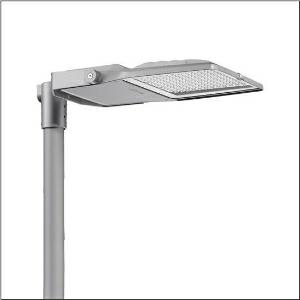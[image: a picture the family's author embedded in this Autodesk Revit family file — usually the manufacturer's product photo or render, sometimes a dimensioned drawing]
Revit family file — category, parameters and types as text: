
# Revit family: floodlight_fl_21_midi___pl64_5xa7785e2e3a_0c5c
name_source: partatom
category: Lighting Fixtures
units: mm (PartAtom-declared; Revit-internal decimal feet)

## family parameters
Cut with Voids When Loaded = No
Host = Face
Light Source = No
Part Type = Normal
Room Calculation Point = No
Round Connector Dimension = Use Diameter
Shared = No

## types (1)
- --- (1 x LED, 26020 lm, 212.4 W, 3000K)
    Apparent Load = 212 VA
    CIE Flux Codes = 28 80 98 100 100
    Color Rendering = 70
    Color Temperature = 3000K
    Default Elevation = 1800 mm
    Description = Floodlight FL 21 midi, floodlight, primary light control with lens, of PMMA, primary optical cover: protective disc, of toughened safety glass, transparent, light distribution: PL64, light emission: direct distribution, installation type: surface-mounted, LED, High Power LED, rated luminous flux: 26.020lm, luminous efficacy: 123lm/W, light colour: 730, colour temperature: 3000K, control gear: Smart Interface (Zhaga), control: flexible luminous flux parameterisation, time-dependent luminous flux control, constant luminous flux control, overheat protection, pre-setting: logarithmic dimming characteristic, with terminal, 6-pole, mains connection: 220..240V, AC, 50/60Hz, start of lifetime: 212W, end of service life: 231W, reduction: 95W, luminaire housing, of diecast aluminium, powder-coated, Siteco® metallic grey (DB 702S), corrosivity category C5 mid according to DIN EN ISO 12944, suitable for swimming pools, chlorine-resistant, sealing non-destructively replaceable, please order mast flange separately, mast bracket, of steel, galvanised, powder-coated, Siteco® metallic grey (DB 702S), Smart Interface above, protection rating (complete): IP66, insulation class (complete): insulation class II (safety insulation), certification: CE, ENEC, VDE, protection symbol: D, impact resistance: IK08, permissible operating ambient temperature: -20..+40°C, permissible operating ambient temperature for outdoor applications: -40..+50°C, standard: DIN EN 12944, LABS conformity tested according to VDMA 24364:2018-05, packaging unit: 1 piece

Light Distribution: PL64
    Height = 76 mm
    Lamp = 1 x LED
    Lamp Light Flux = 26020 lm
    Lamp Power = 212.4 W
    Lamp count = 1
    Length = 657 mm
    Luminous efficacy = 123 lm/W
    Manufacturer = Siteco
    ModVariant = No
    Model = 5XA7785E2E3A
    Number of Poles = 1
    OnlyDefault = Yes
    Power Factor = 1
    Product Name = Floodlight FL 21 midi | PL64
    Product group = floodlight | pylon annexe
    ProductGroupID = 6200
    Protection Class = Protection class II
    Protection Degree = IP 66
    RLX_Detail_Level = 1
    RLX_Emergency_Light_Flux = 0 lm
    RLX_Emergency_Type = 0
    RLX_Emergency_Type_DB = No
    RlxData = <blob elided: 153825 chars, md5=42bfeb22>
    Socket = socket
    Standby Power = 0 W
    System Light Flux = 26020 lm
    System Power = 212 W
    Type Comments = factory setting: luminous flux: 100 % | dim-lin: 254 | 710 mA
    Type Image = l_1007123.jpg
    URL = http://relux.com
    VarID = @adj_180394
    Voltage = 0 V
    Weight = 0.00 kg
    Width = 442 mm

## geometry (parser evidence)
native form markers: Blend x4, Sweep x13
no freeform markers — native parametric forms only
